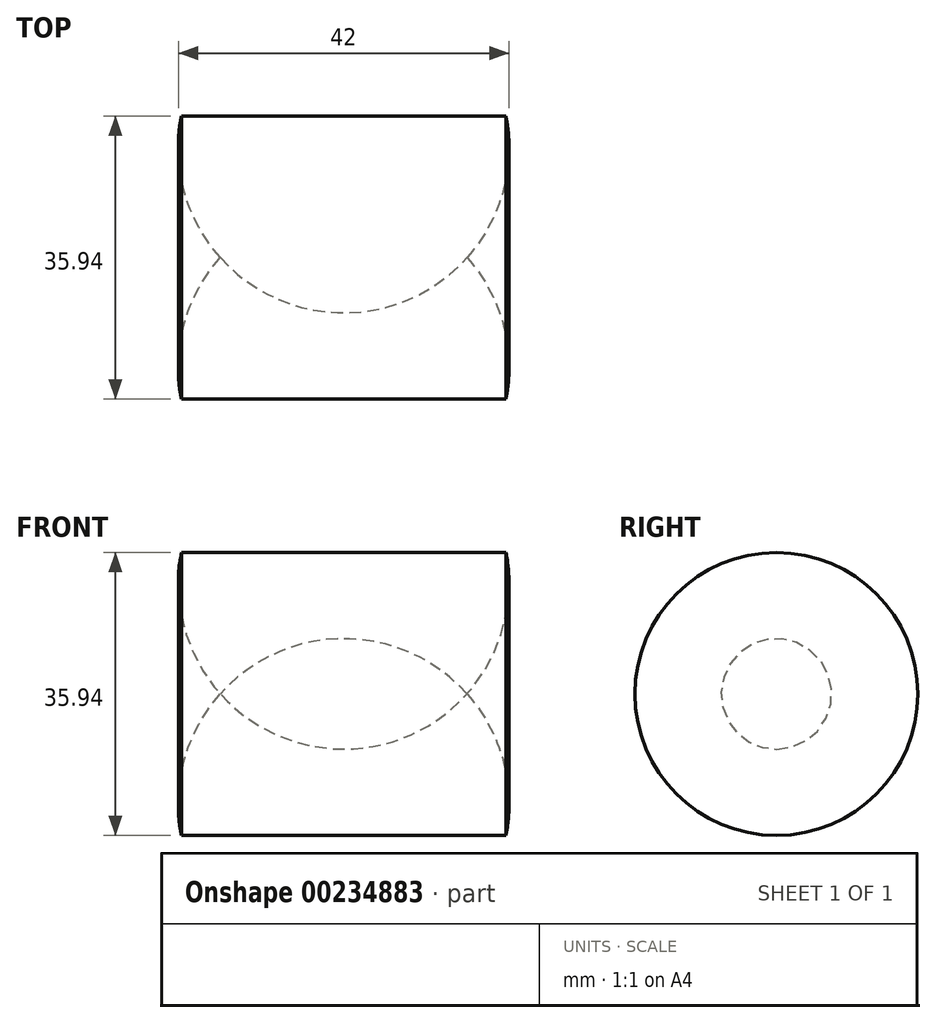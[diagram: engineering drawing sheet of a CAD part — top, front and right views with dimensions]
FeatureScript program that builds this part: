
annotation { "Feature Type Name" : "Feature", "Feature Type Description" : "" }
export const myFeature = defineFeature(function(context is Context, id is Id, definition is map)
    precondition{}
    {
        {
            var Q0;
            Q0=qCreatedBy(makeId("Front.planeOp"),FACE);
            var sketch = newSketch(context, id + "F1", { "sketchPlane" : qUnion([Q0])});
            skArc(sketch, "E0", {"start": v(41.24, 0) * mm, "mid": v(20.62, 17.01) * mm, "end": v(0, 0) * mm});
            skLineSegment(sketch, "E1", {"start": v(-42.1, -17.97) * mm, "end": v(74.4, -17.97) * mm});
            skLineSegment(sketch, "E2", {"start": v(0, 0) * mm, "end": v(41.24, 0) * mm});
            skSolve(sketch);
        }
        {
            var Q0;
            Q0=makeQuery(id+"F1.imprint","IMPRINT",FACE,{"disambiguationData":[TD([[makeQuery(id+"F1.imprint","IMPRINT",EDGE,{"derivedFrom":sQuery(id+"F1.wireOp",EDGE,"E0")}),1.0]])]});
            var Q1;
            Q1=sQuery(id+"F1.wireOp",EDGE,"E1");
            revolve(context, id + "F0", {"entities" : qUnion([Q0]), "axis" : qUnion([Q1]), "revolveType" : RevolveType.FULL});
        }
    });
